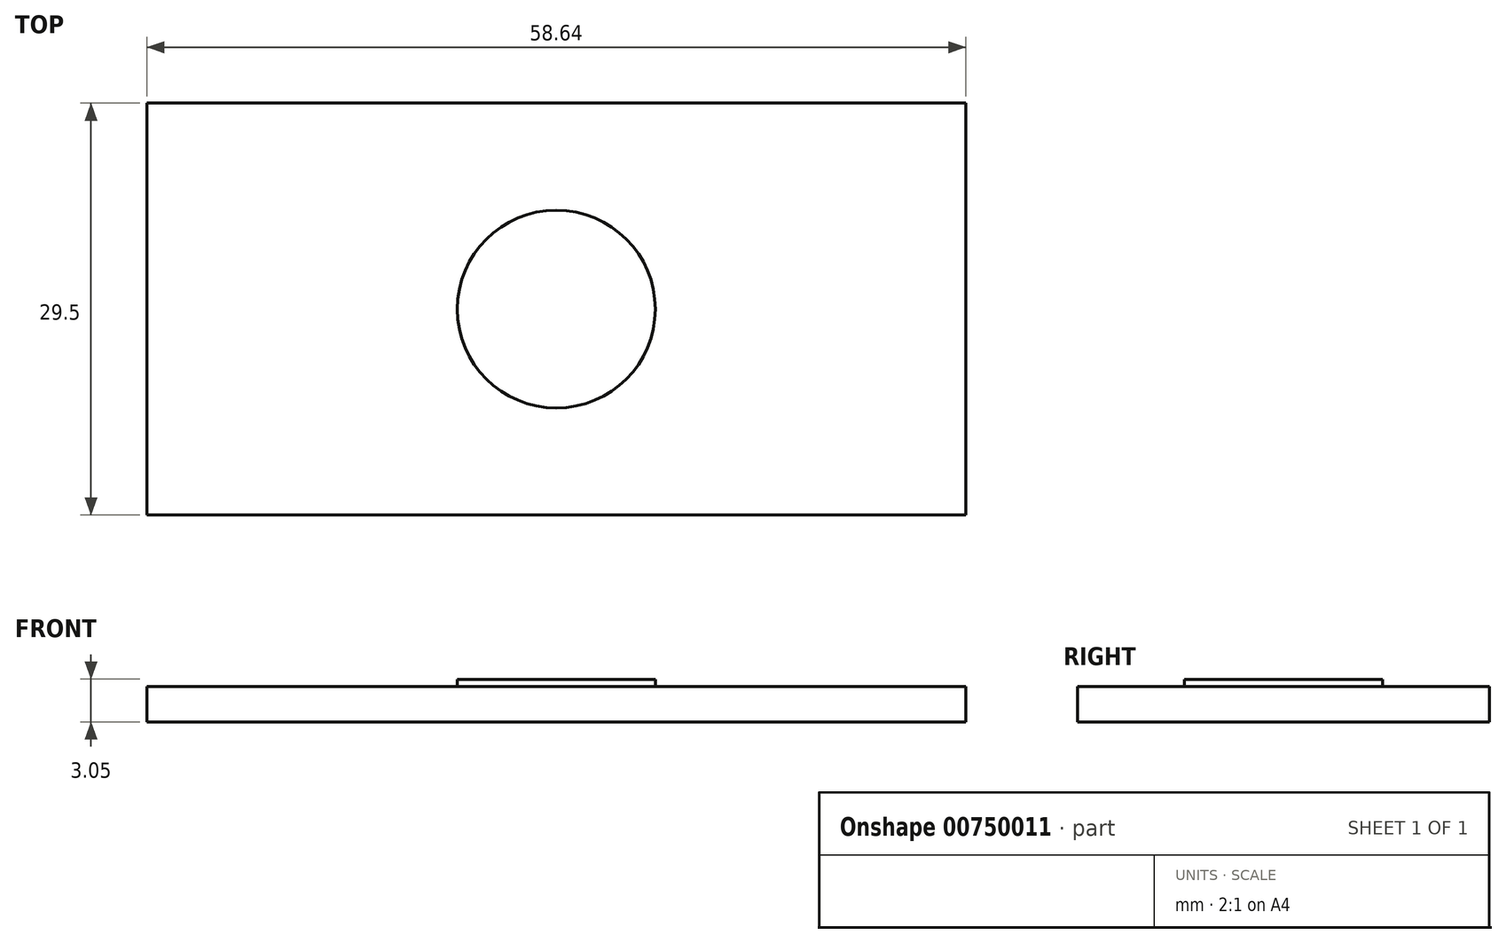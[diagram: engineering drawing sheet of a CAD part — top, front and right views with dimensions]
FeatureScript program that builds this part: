
annotation { "Feature Type Name" : "Feature", "Feature Type Description" : "" }
export const myFeature = defineFeature(function(context is Context, id is Id, definition is map)
    precondition{}
    {
        {
            var Q0;
            Q0=qCreatedBy(makeId("Top.planeOp"),FACE);
            var sketch = newSketch(context, id + "F0", { "sketchPlane" : qUnion([Q0])});
            skLineSegment(sketch, "E0.bottom", {"start": v(-29.32, 14.75) * mm, "end": v(29.32, 14.75) * mm});
            skLineSegment(sketch, "E0.top", {"start": v(-29.32, -14.75) * mm, "end": v(29.32, -14.75) * mm});
            skLineSegment(sketch, "E0.left", {"start": v(-29.32, 14.75) * mm, "end": v(-29.32, -14.75) * mm});
            skLineSegment(sketch, "E0.right", {"start": v(29.32, 14.75) * mm, "end": v(29.32, -14.75) * mm});
            skPoint(sketch, "E0.middle", {"position": v(0, 0) * mm});
            skSolve(sketch);
        }
        {
            var Q0;
            Q0=makeQuery(id+"F0.imprint","IMPRINT",FACE,{"disambiguationData":[TD([[makeQuery(id+"F0.imprint","IMPRINT",EDGE,{"derivedFrom":sQuery(id+"F0.wireOp",EDGE,"E0.bottom")}),-1.0]])]});
            extrude(context, id + "F1", {"entities" : qUnion([Q0]), "depth" : 2.54 * mm, "offsetDistance" : 25.4 * mm});
        }
        {
            var Q0;
            Q0=qCreatedBy(makeId("Top.planeOp"),FACE);
            var sketch = newSketch(context, id + "F2", { "sketchPlane" : qUnion([Q0])});
            skCircle(sketch, "E1", {"center": v(0, 0) * mm, "radius": 7.09 * mm});
            skSolve(sketch);
        }
        {
            var Q0;
            Q0 = qSketchRegion(id + "F2", true);
            extrude(context, id + "F3", {"entities" : qUnion([Q0]), "operationType" : NewBodyOperationType.ADD, "depth" : 3.05 * mm, "offsetDistance" : 25.4 * mm});
        }
    });
